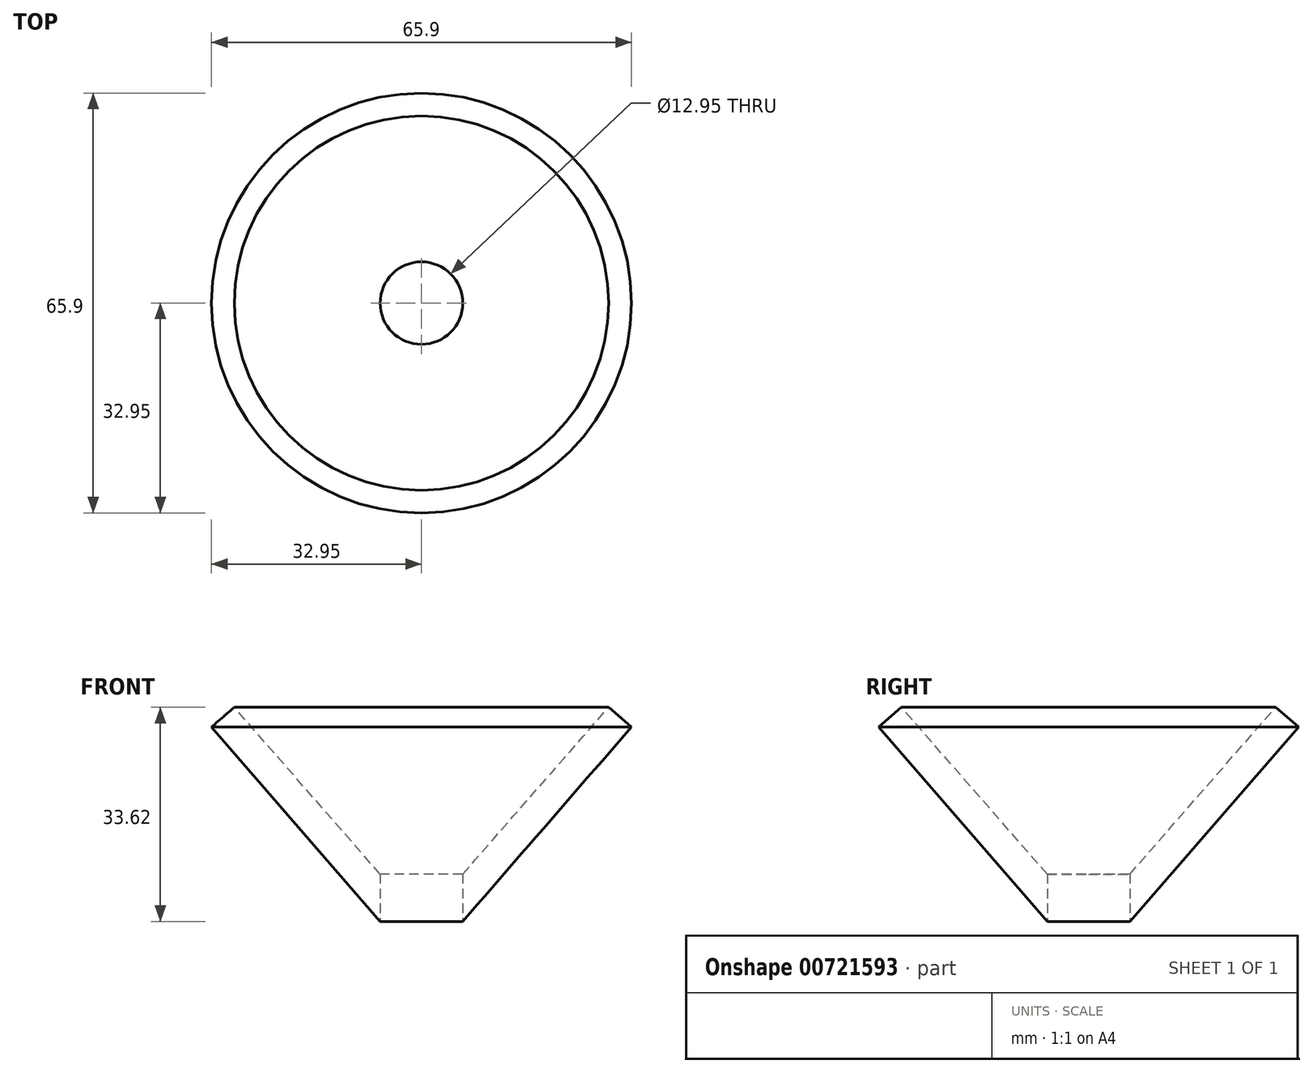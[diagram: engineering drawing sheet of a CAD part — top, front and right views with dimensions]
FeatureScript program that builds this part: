
annotation { "Feature Type Name" : "Feature", "Feature Type Description" : "" }
export const myFeature = defineFeature(function(context is Context, id is Id, definition is map)
    precondition{}
    {
        {
            var Q0;
            Q0=qCreatedBy(makeId("Front.planeOp"),FACE);
            var sketch = newSketch(context, id + "F0", { "sketchPlane" : qUnion([Q0])});
            skLineSegment(sketch, "E0", {"start": v(0, 0) * mm, "end": v(0, 9.35) * mm});
            skLineSegment(sketch, "E1", {"start": v(0, 9.35) * mm, "end": v(6.48, 9.35) * mm});
            skLineSegment(sketch, "E2", {"start": v(6.48, 9.35) * mm, "end": v(6.48, 0) * mm});
            skLineSegment(sketch, "E3", {"start": v(6.48, 0) * mm, "end": v(0, 0) * mm});
            skLineSegment(sketch, "E4", {"start": v(6.48, 9.35) * mm, "end": v(32.95, 39.86) * mm});
            skLineSegment(sketch, "E5", {"start": v(32.95, 39.86) * mm, "end": v(29.37, 42.97) * mm});
            skLineSegment(sketch, "E6", {"start": v(29.37, 42.97) * mm, "end": v(0, 9.35) * mm});
            skSolve(sketch);
        }
        {
            var Q0;
            Q0 = qSketchRegion(id + "F0", true);
            var Q1;
            Q1=sQuery(id+"F0.wireOp",EDGE,"E0");
            revolve(context, id + "F1", {"surfaceOperationType" : NewSurfaceOperationType.NEW, "entities" : qUnion([Q0]), "axis" : qUnion([Q1]), "revolveType" : RevolveType.FULL});
        }
        {
            var Q0;
            Q0=makeQuery(id+"F1.opRevolve","SWEPT_FACE",FACE,{"disambiguationData":[OSD([sQuery(id+"F0.wireOp",EDGE,"E3")])]});
            extrude(context, id + "F2", {"entities" : qUnion([Q0]), "operationType" : NewBodyOperationType.REMOVE, "oppositeDirection" : true, "depth" : 25.4 * mm, "offsetDistance" : 25.4 * mm});
        }
    });
